# Revit family: VITOCAL 200-A PRO AWO-AC 204.A128 EN
name_source: partatom
category: Mechanical Equipment
units: mm (PartAtom-declared; Revit-internal decimal feet)

## family parameters
Always vertical = Yes
Cut with Voids When Loaded = No
OmniClass Number = 23.75.10.21.17
OmniClass Title = Water-Source Heat Pumps
Part Type = Normal
Room Calculation Point = No
Round Connector Dimension = Use Diameter
Shared = No
Work Plane-Based = No

## types (1)
- VITOCAL 200-A PRO AWO-AC 204.A128
    Art of color = Viessmann color 1
    Art of electrical protection = IPX4
    COP factor of efficiency (heating mode) = 4.05
    Compressor. Compressor inrush current (A) = 2 x 122.7 A
    Compressor. Cosine of electric current φ = 0.75
    Compressor. Max. cross-section of electrical connecting cables (mm2) = 16 mm2
    Compressor. Maximal operating current (A) = 2 x 53,4
    Compressor. Maximal power consumption of the compressor (for parameters A2/W35, including fans) (kWe) = 2 x 14.600 kW
    Compressor. Rated voltage (v) = 3/N/PE 400 V/50 Hz
    Compressor. Required security of electrical connection = i 3 x C63A Kombi
    Default Elevation = 0 mm  [stored 0 ft]
    Description = The Vitocal 200-A PRO heat pump extracts heat energy from the outside air and uses it for heating water in the heating circuit or domestic hot water circuit or in cooling mode - extracts heat from the building and releases it to the outside air.
Thanks to the air heater (evaporator) thermal energy, coming from the outside air constantly sucked in by the fan, is returned to the working medium (refrigerant - freon R407c). In the process, the refrigerant evaporates, with the help of an electrically driven compressor the temperature of the gaseous refrigerant is increased. In the so-called condenser, the refrigerant (R407c) is condensed again and can be fed back into the evaporator through the expansion valve.
After evaporation and condensation, the heat energy from the refrigerant through condensation in the heat exchanger is transferred to the heating or cooling medium (water or glycol), and then to the buffer tank (not included in the scope of delivery) and then to the heating/or cooling system in building.
Warning : 
- At low ambient temperatures, moisture accumulates in the evaporator as frost, which adversely affects the heat transfer. If necessary, the evaporator is automatically defrosted by the heat pump. Depending on the weather conditions, steam may be generated in the air outlet. Depending on the regional conditions, it is necessary to optimized unit during operation.
- To ensure sound insulation, the unit must be connected via flexible hydraulic pipe connections.
    EER factor (cooling mode) = 5.23
    Electric power (kWe) for oilsump heating = 4 x 90
    Electrical Power consumption (kWe) = 27.8 kW
    Heat intake from outside air. Amount of condensation water at 87% humidity = 60
    Heat intake from outside air. Maximal electrical power of fan(s) = 8 x 500 W
    Heat intake from outside air. Maximal inlet air temperature = 35 °C
    Heat intake from outside air. Minimal inlet air temperature = –20 °C
    Heat intake from outside air. Nominal volumetric air flow (m3/h) = 19 100 m3/h
    Heating water. Flow Resistances of minimum volumetric flow = 2.9
    Heating water. Flow Resistances of nominal volumetric flow = 7.1
    Heating water. Maximal supply temperature (Outlet from device) = 65 °C
    Heating water. Minimal return temperature (Inlet to device) = 20 °C
    Heating water. Minimum volumetric flow (by 1 compressor running) = 2800 l/h
    Heating water. Nominal volumetric flow = 19 380 l/h
    Heating water. Water capacity of device = 17.3 l
    Height (overall) = 2265 mm  [stored 7.4311 ft]
    Hydraulic connections. Heating water supply and return (external thread) = G 2½
    Information = Measurement of total sound power level based on standard EN ISO 12102/EN ISO 9614.
    Length (overall) = 2130 mm  [stored 6.98819 ft]
    Low temperature application (W35). LT Energy efficiency ηS (%) = 173
    Low temperature application (W35). Rated heating power / P-rated (kWt) = 99
    Low temperature application (W35). Seasonal efficiency rating (SCOP) = 4.4
    Manufacturer = Viessmann Sp. z o.o.
    Maximum operating pressure (water side) = 6 bar
    Medium temperature application (W55). MT Energy efficiency ηS  (%) = 129
    Medium temperature application (W55). Rated heating power P-rated (kWt) = 108
    Medium temperature application (W55). Seasonal efficiency rating (SCOP) = 3.29
    Model = Air-to-water heat pumps with electic compressor, outdoor instalation, for space heating and domestic hot water heating in small and medium-sized commercial buildings: 
- Up to +65°C supply water temperature, 
- Depending on the type, with 1, 2 or 4 compressors, 
- With weather-controlled heating controller and graphical control module for wall mounting.
    Nominal cooling power (kWt) = 139.9 kW
    Nominal heating power (kWt) = 112.4 kW
    Refrigeration circuit. Amount of oil in the compressor(s) = 2.8
    Refrigeration circuit. CO2 equivalent = 76.3
    Refrigeration circuit. Compressor = Scroll
    Refrigeration circuit. Global Warming Potential (GWP) = 1774
    Refrigeration circuit. Refrigerant medium = R407C
    Refrigeration circuit. Refrigerant quantity in the device = 43.00 kg
    Refrigeration circuit. Safety fittings = A1
    Refrigeration circuit. Type of oil in the compressor = Idemitsu FV68S
    Sound power level (dBA) = 71.6 dB(A)
    Total weight (basic unit without options) = 1850.00 kg
    URL = https://www.viessmann.pl
    Ventilator. Internal security = B10A
    Ventilator. Maximal electrical power consumption per 1 fan (kWe) = 500 W
    Ventilator. Rated voltage (v) = 1/N/PE 230 V/50 Hz
    Width (overall) = 2280 mm  [stored 7.48031 ft]

note: source unit labels omitted for Heating water. Flow Resistances of minimum volumetric flow, Heating water. Flow Resistances of nominal volumetric flow — the stored unit's dimension contradicts the parameter name (converter mislabeling)

note: [stored X ft] marks values corroborated as IEEE doubles in the binary element streams (Revit-internal decimal feet)
